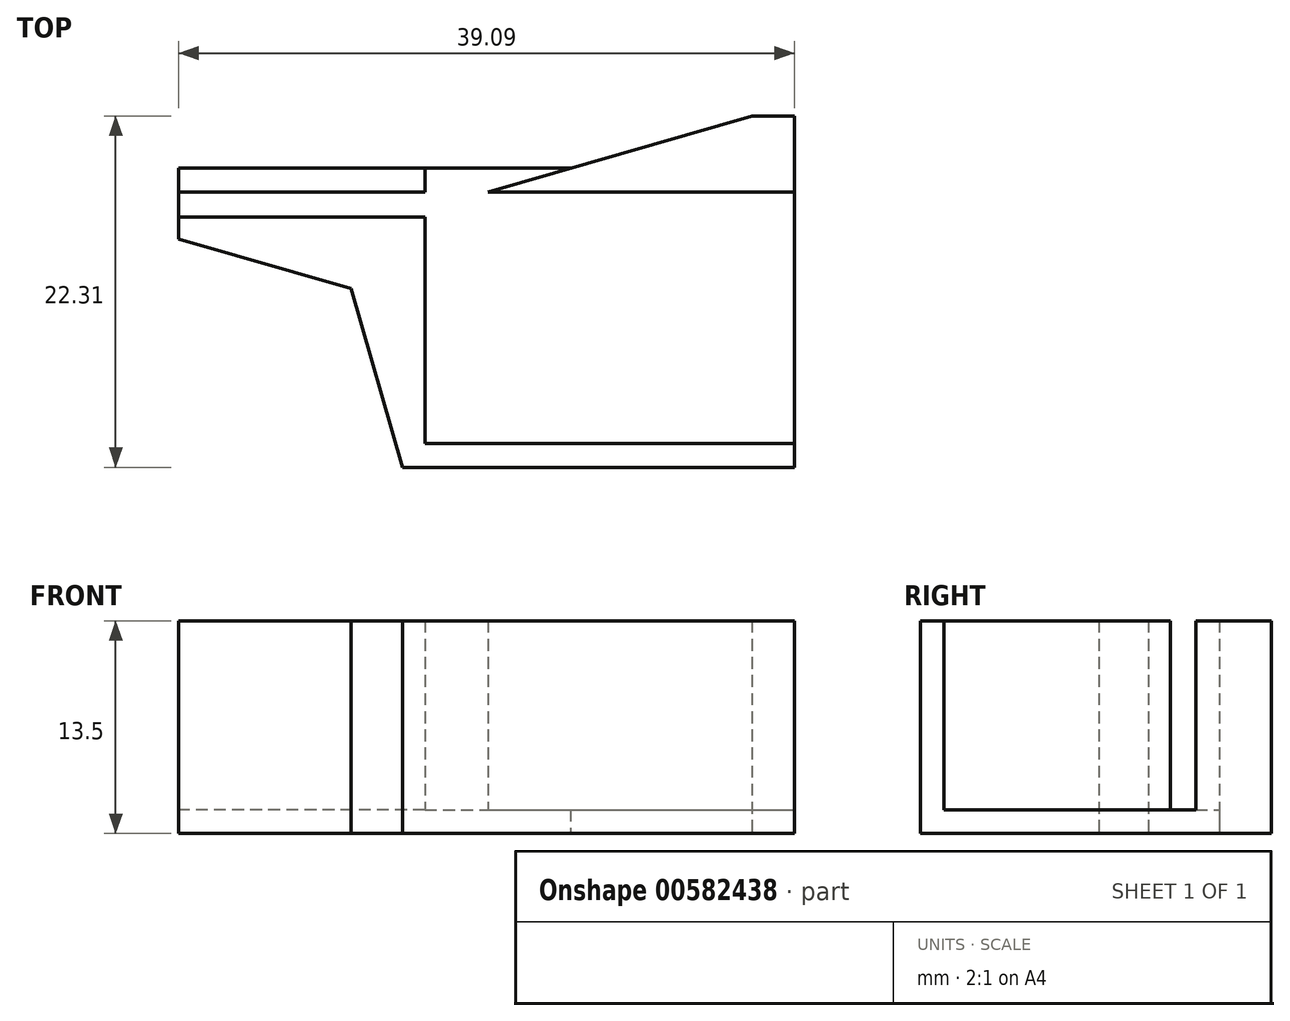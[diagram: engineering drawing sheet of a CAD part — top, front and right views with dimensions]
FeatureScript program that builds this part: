
annotation { "Feature Type Name" : "Feature", "Feature Type Description" : "" }
export const myFeature = defineFeature(function(context is Context, id is Id, definition is map)
    precondition{}
    {
        {
            var Q0;
            Q0=qCreatedBy(makeId("Top.planeOp"),FACE);
            var sketch = newSketch(context, id + "F0", { "sketchPlane" : qUnion([Q0])});
            skLineSegment(sketch, "E0", {"start": v(-29.96, 12.16) * mm, "end": v(-5.1, 12.16) * mm});
            skLineSegment(sketch, "E1", {"start": v(-5.1, 12.16) * mm, "end": v(6.44, 15.47) * mm});
            skLineSegment(sketch, "E2", {"start": v(6.44, 15.47) * mm, "end": v(9.13, 15.47) * mm});
            skLineSegment(sketch, "E3", {"start": v(9.13, 15.47) * mm, "end": v(9.13, -6.84) * mm});
            skLineSegment(sketch, "E4", {"start": v(9.13, -6.84) * mm, "end": v(-15.76, -6.84) * mm});
            skLineSegment(sketch, "E5", {"start": v(-15.76, -6.84) * mm, "end": v(-19.02, 4.52) * mm});
            skLineSegment(sketch, "E6", {"start": v(-19.02, 4.52) * mm, "end": v(-29.96, 7.66) * mm});
            skLineSegment(sketch, "E7", {"start": v(-29.96, 7.66) * mm, "end": v(-29.96, 12.16) * mm});
            skSolve(sketch);
        }
        {
            var Q0;
            Q0=makeQuery(id+"F0.imprint","IMPRINT",FACE,{"disambiguationData":[TD([[makeQuery(id+"F0.imprint","IMPRINT",EDGE,{"derivedFrom":sQuery(id+"F0.wireOp",EDGE,"E0")}),-1.0]])]});
            extrude(context, id + "F1", {"entities" : qUnion([Q0]), "depth" : 1.5 * mm, "offsetDistance" : 25 * mm});
        }
        {
            var Q0;
            Q0=makeQuery(id+"F1.opExtrude","CAP_FACE",FACE,{"disambiguationData":[OSD([sQuery(id+"F0.wireOp",EDGE,"E0"),sQuery(id+"F0.wireOp",EDGE,"E1"),sQuery(id+"F0.wireOp",EDGE,"E2"),sQuery(id+"F0.wireOp",EDGE,"E3"),sQuery(id+"F0.wireOp",EDGE,"E4"),sQuery(id+"F0.wireOp",EDGE,"E5"),sQuery(id+"F0.wireOp",EDGE,"E6"),sQuery(id+"F0.wireOp",EDGE,"E7")])],"isStart":false});
            var sketch = newSketch(context, id + "F2", { "sketchPlane" : qUnion([Q0])});
            skLineSegment(sketch, "E8", {"start": v(-29.96, 7.66) * mm, "end": v(-29.96, 9.06) * mm});
            skLineSegment(sketch, "E9", {"start": v(-29.96, 9.06) * mm, "end": v(-14.32, 9.06) * mm});
            skLineSegment(sketch, "E10", {"start": v(-14.32, 9.06) * mm, "end": v(-14.32, -5.34) * mm});
            skLineSegment(sketch, "E11", {"start": v(-14.32, -5.34) * mm, "end": v(9.13, -5.34) * mm});
            skLineSegment(sketch, "E12", {"start": v(9.13, -5.34) * mm, "end": v(9.13, -6.84) * mm});
            skLineSegment(sketch, "E13", {"start": v(9.13, -6.84) * mm, "end": v(-15.76, -6.84) * mm});
            skLineSegment(sketch, "E14", {"start": v(-15.76, -6.84) * mm, "end": v(-19.02, 4.52) * mm});
            skLineSegment(sketch, "E15", {"start": v(-19.02, 4.52) * mm, "end": v(-29.96, 7.66) * mm});
            skLineSegment(sketch, "E16", {"start": v(-29.96, 12.16) * mm, "end": v(-14.32, 12.16) * mm});
            skLineSegment(sketch, "E17", {"start": v(-14.32, 12.16) * mm, "end": v(-14.32, 10.66) * mm});
            skLineSegment(sketch, "E18", {"start": v(-14.32, 10.66) * mm, "end": v(-29.96, 10.66) * mm});
            skLineSegment(sketch, "E19", {"start": v(-29.96, 10.66) * mm, "end": v(-29.96, 12.16) * mm});
            skLineSegment(sketch, "E20", {"start": v(6.44, 15.47) * mm, "end": v(-5.1, 12.16) * mm});
            skLineSegment(sketch, "E21", {"start": v(-5.1, 12.16) * mm, "end": v(-10.32, 10.66) * mm});
            skPoint(sketch, "E22.endSnap0", {"position": v(-7.7, 11.41) * mm});
            skLineSegment(sketch, "E23", {"start": v(9.13, 15.47) * mm, "end": v(6.44, 15.47) * mm});
            skLineSegment(sketch, "E24", {"start": v(-10.32, 10.66) * mm, "end": v(9.13, 10.66) * mm});
            skLineSegment(sketch, "E25", {"start": v(9.13, 10.66) * mm, "end": v(9.13, 15.47) * mm});
            skSolve(sketch);
        }
        {
            var Q0;
            Q0=makeQuery(id+"F2.imprint","IMPRINT",FACE,{"disambiguationData":[TD([[makeQuery(id+"F2.imprint","IMPRINT",EDGE,{"derivedFrom":sQuery(id+"F2.wireOp",EDGE,"E8")}),-1.0]])]});
            var Q1;
            Q1=makeQuery(id+"F2.imprint","IMPRINT",FACE,{"disambiguationData":[TD([[makeQuery(id+"F2.imprint","IMPRINT",EDGE,{"derivedFrom":sQuery(id+"F2.wireOp",EDGE,"E16")}),-1.0]])]});
            var Q2;
            Q2=makeQuery(id+"F2.imprint","IMPRINT",FACE,{"disambiguationData":[TD([[makeQuery(id+"F2.imprint","IMPRINT",EDGE,{"derivedFrom":sQuery(id+"F2.wireOp",EDGE,"E20")}),-1.0]])]});
            extrude(context, id + "F3", {"entities" : qUnion([Q0, Q1, Q2]), "operationType" : NewBodyOperationType.ADD, "depth" : 12 * mm, "offsetDistance" : 25 * mm});
        }
    });
